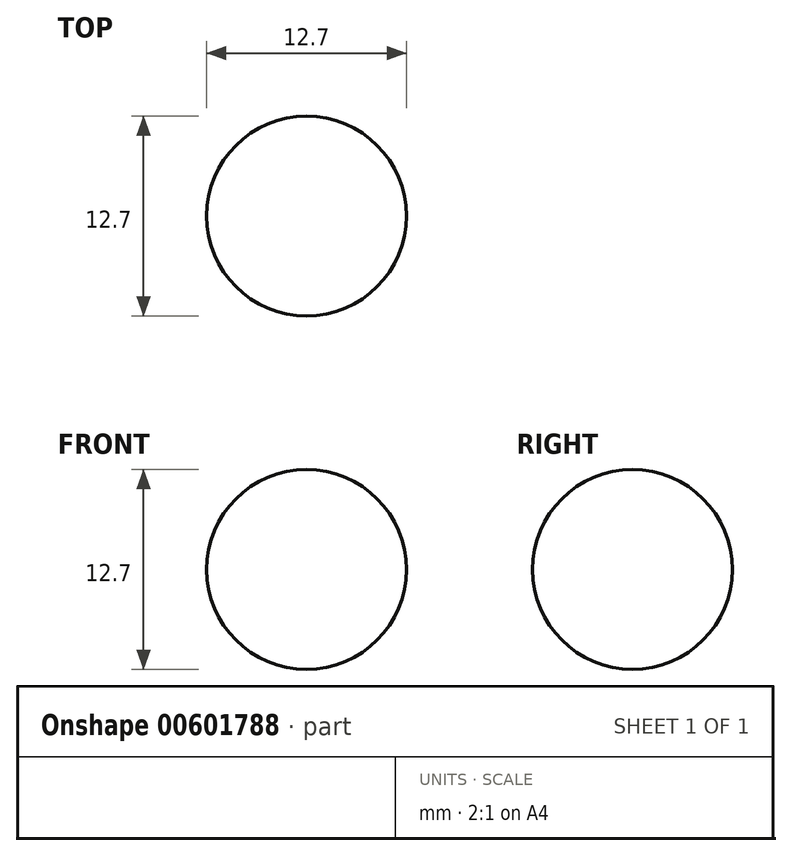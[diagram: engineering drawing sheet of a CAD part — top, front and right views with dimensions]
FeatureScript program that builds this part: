
annotation { "Feature Type Name" : "Feature", "Feature Type Description" : "" }
export const myFeature = defineFeature(function(context is Context, id is Id, definition is map)
    precondition{}
    {
        {
            var Q0;
            Q0=qCreatedBy(makeId("Front.planeOp"),FACE);
            var sketch = newSketch(context, id + "F0", { "sketchPlane" : qUnion([Q0])});
            skCircle(sketch, "E0", {"center": v(0, 0) * mm, "radius": 6.35 * mm});
            skLineSegment(sketch, "E1", {"start": v(0, 6.35) * mm, "end": v(0, -6.35) * mm});
            skSolve(sketch);
        }
        {
            var Q0;
            {var subQ0=sQuery(id+"F0.wireOp",EDGE,"E1");Q0=makeQuery(id+"F0.imprint","IMPRINT",FACE,{"disambiguationData":[TD([[makeQuery(id+"F0.imprint","IMPRINT",EDGE,{"derivedFrom":subQ0}),1.0]])]});}
            var Q1;
            Q1=sQuery(id+"F0.wireOp",EDGE,"E1");
            revolve(context, id + "F1", {"entities" : qUnion([Q0]), "axis" : qUnion([Q1]), "revolveType" : RevolveType.FULL});
        }
    });
